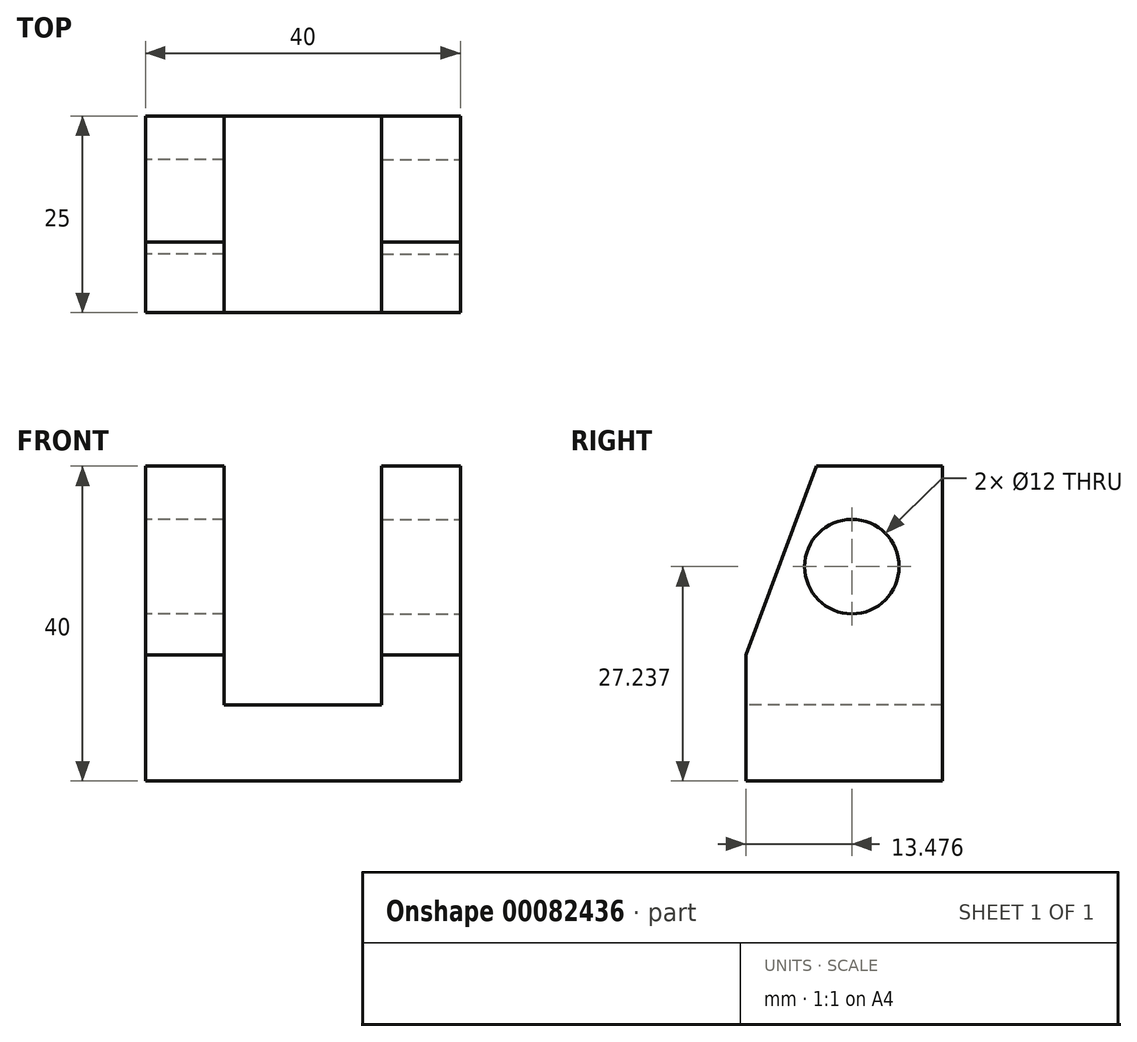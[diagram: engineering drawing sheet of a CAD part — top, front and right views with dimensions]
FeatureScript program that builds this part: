
annotation { "Feature Type Name" : "Feature", "Feature Type Description" : "" }
export const myFeature = defineFeature(function(context is Context, id is Id, definition is map)
    precondition{}
    {
        {
            var Q0;
            Q0=qCreatedBy(makeId("Front.planeOp"),FACE);
            var sketch = newSketch(context, id + "F0", { "sketchPlane" : qUnion([Q0])});
            skLineSegment(sketch, "E0", {"start": v(10, 0) * mm, "end": v(10, 30.31) * mm});
            skLineSegment(sketch, "E1", {"start": v(10, 30.31) * mm, "end": v(20, 30.31) * mm});
            skLineSegment(sketch, "E2", {"start": v(20, 30.31) * mm, "end": v(20, -9.69) * mm});
            skLineSegment(sketch, "E3", {"start": v(20, -9.69) * mm, "end": v(0, -9.69) * mm});
            skLineSegment(sketch, "E4", {"start": v(0, -9.69) * mm, "end": v(0, 0) * mm});
            skLineSegment(sketch, "E5", {"start": v(0, 0) * mm, "end": v(10, 0) * mm});
            skSolve(sketch);
        }
        {
            var Q0;
            Q0=makeQuery(id+"F0.imprint","IMPRINT",FACE,{"disambiguationData":[TD([[makeQuery(id+"F0.imprint","IMPRINT",EDGE,{"derivedFrom":sQuery(id+"F0.wireOp",EDGE,"E0")}),-1.0]])]});
            extrude(context, id + "F1", {"entities" : qUnion([Q0]), "oppositeDirection" : true, "depth" : 25 * mm});
        }
        {
            var Q0;
            Q0=makeQuery(id+"F1.opExtrude","SWEPT_FACE",FACE,{"disambiguationData":[OSD([sQuery(id+"F0.wireOp",EDGE,"E2")])]});
            var sketch = newSketch(context, id + "F2", { "sketchPlane" : qUnion([Q0])});
            skPoint(sketch, "E6", {"position": v(13.48, 17.55) * mm});
            skSolve(sketch);
        }
        {
            var Q0;
            Q0=sQuery(id+"F2.wireOp",VERTEX,"E6");
            var Q1;
            Q1=makeQuery(id+"F1.opExtrude","SWEPT_BODY",BODY,{"disambiguationData":[OSD([sQuery(id+"F0.wireOp",EDGE,"E0"),sQuery(id+"F0.wireOp",EDGE,"E1"),sQuery(id+"F0.wireOp",EDGE,"E2"),sQuery(id+"F0.wireOp",EDGE,"E3"),sQuery(id+"F0.wireOp",EDGE,"E4"),sQuery(id+"F0.wireOp",EDGE,"E5")])]});
            hole(context, id + "F3", {"style" : HoleStyle.SIMPLE, "endStyle" : HoleEndStyle.THROUGH, "holeDiameter" : 12 * mm, "locations" : qUnion([Q0]), "scope" : qUnion([Q1]), "isTappedThrough" : true});
        }
        {
            var Q0;
            Q0=makeQuery(id+"F1.opExtrude","CAP_EDGE",EDGE,{"disambiguationData":[OSD([sQuery(id+"F0.wireOp",EDGE,"E1")])],"isStart":true});
            chamfer(context, id + "F4", {"entities" : qUnion([Q0]), "chamferType" : ChamferType.TWO_OFFSETS, "width1" : 9 * mm, "oppositeDirection" : false, "width2" : 24 * mm, "tangentPropagation" : true});
        }
        {
            var Q0;
            Q0=makeQuery(id+"F1.opExtrude","SWEPT_BODY",BODY,{"disambiguationData":[OSD([sQuery(id+"F0.wireOp",EDGE,"E0"),sQuery(id+"F0.wireOp",EDGE,"E1"),sQuery(id+"F0.wireOp",EDGE,"E2"),sQuery(id+"F0.wireOp",EDGE,"E3"),sQuery(id+"F0.wireOp",EDGE,"E4"),sQuery(id+"F0.wireOp",EDGE,"E5")])]});
            var Q1;
            Q1=qCreatedBy(makeId("Right.planeOp"),FACE);
            mirror(context, id + "F5", {"operationType" : NewBodyOperationType.ADD, "entities" : qUnion([Q0]), "mirrorPlane" : qUnion([Q1])});
        }
    });
